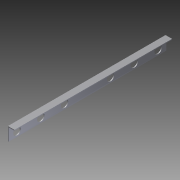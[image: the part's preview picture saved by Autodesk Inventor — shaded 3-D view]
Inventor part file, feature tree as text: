
AUTODESK INVENTOR PART (.ipt)
format: ipt  version: 2012 (Build 160160000, 160)  size: 96,256 bytes
history: native  units: in
note: dims shown in document units (in); Inventor stores cm internally (conversion verified against a paired STEP export)
features: extrude x2, sketch x2
ambient origin geometry x8: Origin, YZ Plane, XZ Plane, XY Plane, X Axis, Y Axis, Z Axis, Center Point
bodies: Solid1 (feature_tree)
feature tree (4):
  extrude  "Extrusion1"  Depth=1.0in
  extrude  "Extrusion2"  Depth=0.125in
  sketch  "Sketch1"  dims[d0=2.0in d1=1.0in]
  sketch  "Sketch2"  dims[d2=0.125in d3=0.125in d4=24.0in d5=0.0in d6=1.125in d7=1.25in d8=0.75in d9=1.125in d10=7.0in d11=1.25in d13=24.25in d14=0.0in d15=7.25in d16=3.625in d17=3.625in d18=24.0in]
